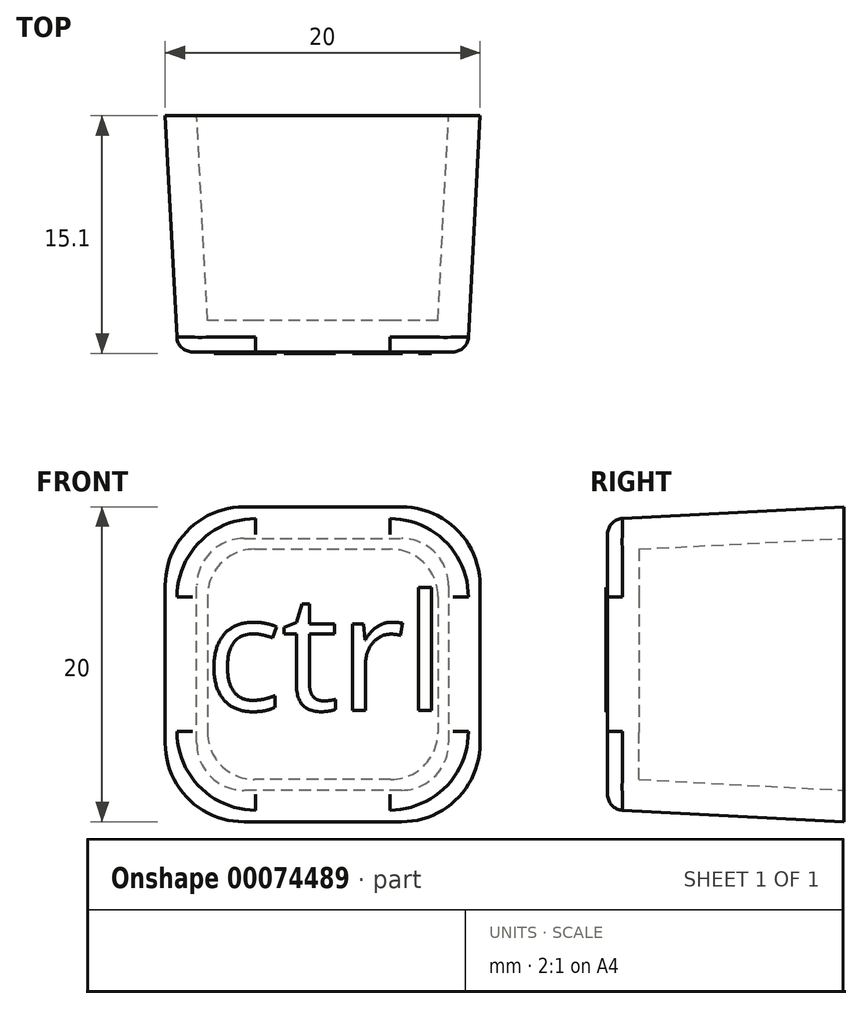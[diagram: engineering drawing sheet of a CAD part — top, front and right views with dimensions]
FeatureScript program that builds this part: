
annotation { "Feature Type Name" : "Feature", "Feature Type Description" : "" }
export const myFeature = defineFeature(function(context is Context, id is Id, definition is map)
    precondition{}
    {
        {
            var Q0;
            Q0=qCreatedBy(makeId("Front.planeOp"),FACE);
            var sketch = newSketch(context, id + "F0", { "sketchPlane" : qUnion([Q0])});
            skLineSegment(sketch, "E0.bottom", {"start": v(23.74, 16.78) * mm, "end": v(43.74, 16.78) * mm});
            skLineSegment(sketch, "E0.top", {"start": v(23.74, 36.78) * mm, "end": v(43.74, 36.78) * mm});
            skLineSegment(sketch, "E0.left", {"start": v(23.74, 16.78) * mm, "end": v(23.74, 36.78) * mm});
            skLineSegment(sketch, "E0.right", {"start": v(43.74, 16.78) * mm, "end": v(43.74, 36.78) * mm});
            skSolve(sketch);
        }
        {
            var Q0;
            Q0 = qSketchRegion(id + "F0", true);
            extrude(context, id + "F1", {"entities" : qUnion([Q0]), "depth" : 15 * mm, "hasDraft" : true, "draftAngle" : 3 * degree, "draftPullDirection" : true});
        }
        {
            var Q0;
            Q0=makeQuery(id+"F1.opExtrude","SWEPT_EDGE",EDGE,{"disambiguationData":[OSD([sQuery(id+"F0.wireOp",EDGE,"E0.bottom"),sQuery(id+"F0.wireOp",EDGE,"E0.right")])]});
            var Q1;
            Q1=makeQuery(id+"F1.opExtrude","SWEPT_EDGE",EDGE,{"disambiguationData":[OSD([sQuery(id+"F0.wireOp",EDGE,"E0.bottom"),sQuery(id+"F0.wireOp",EDGE,"E0.left")])]});
            var Q2;
            Q2=makeQuery(id+"F1.opExtrude","SWEPT_EDGE",EDGE,{"disambiguationData":[OSD([sQuery(id+"F0.wireOp",EDGE,"E0.top"),sQuery(id+"F0.wireOp",EDGE,"E0.left")])]});
            var Q3;
            Q3=makeQuery(id+"F1.opExtrude","SWEPT_EDGE",EDGE,{"disambiguationData":[OSD([sQuery(id+"F0.wireOp",EDGE,"E0.top"),sQuery(id+"F0.wireOp",EDGE,"E0.right")])]});
            fillet(context, id + "F2", {"entities" : qUnion([Q0, Q1, Q2, Q3]), "radius" : 5 * mm, "tangentPropagation" : true, "allowEdgeOverflow" : false});
        }
        {
            var Q0;
            Q0=makeQuery(id+"F1.opExtrude","CAP_FACE",FACE,{"disambiguationData":[OSD([sQuery(id+"F0.wireOp",EDGE,"E0.bottom"),sQuery(id+"F0.wireOp",EDGE,"E0.top"),sQuery(id+"F0.wireOp",EDGE,"E0.left"),sQuery(id+"F0.wireOp",EDGE,"E0.right")])],"isStart":false});
            fillet(context, id + "F6", {"entities" : qUnion([Q0]), "radius" : 1 * mm, "tangentPropagation" : true, "allowEdgeOverflow" : false});
        }
        {
            var Q0;
            Q0=makeQuery(id+"F1.opExtrude","CAP_FACE",FACE,{"disambiguationData":[OSD([sQuery(id+"F0.wireOp",EDGE,"E0.bottom"),sQuery(id+"F0.wireOp",EDGE,"E0.top"),sQuery(id+"F0.wireOp",EDGE,"E0.left"),sQuery(id+"F0.wireOp",EDGE,"E0.right")])],"isStart":true});
            shell(context, id + "F3", {"entities" : qUnion([Q0]), "thickness" : 2 * mm});
        }
        {
            var Q0;
            Q0=makeQuery(id+"F1.opExtrude","CAP_FACE",FACE,{"disambiguationData":[OSD([sQuery(id+"F0.wireOp",EDGE,"E0.bottom"),sQuery(id+"F0.wireOp",EDGE,"E0.top"),sQuery(id+"F0.wireOp",EDGE,"E0.left"),sQuery(id+"F0.wireOp",EDGE,"E0.right")])],"isStart":false});
            var sketch = newSketch(context, id + "F4", { "sketchPlane" : qUnion([Q0])});
            skText(sketch, "E1", { "text": "ctrl", "fontName": "OpenSans-Regular.ttf"});
            skPoint(sketch, "E1.secondSnap0", {"position": v(32.16, 31.25) * mm});
            skPoint(sketch, "E2", {"position": v(40.83, 25.35) * mm});
            const initialGuessF4  = {"E1": [0.02626, 0.02387, 1, 0, 0.00738]};
            skSetInitialGuess(sketch, initialGuessF4);
            skSolve(sketch);
        }
        {
            var Q0;
            Q0 = qSketchRegion(id + "F4", true);
            extrude(context, id + "F5", {"entities" : qUnion([Q0]), "depth" : .1 * mm});
        }
    });
